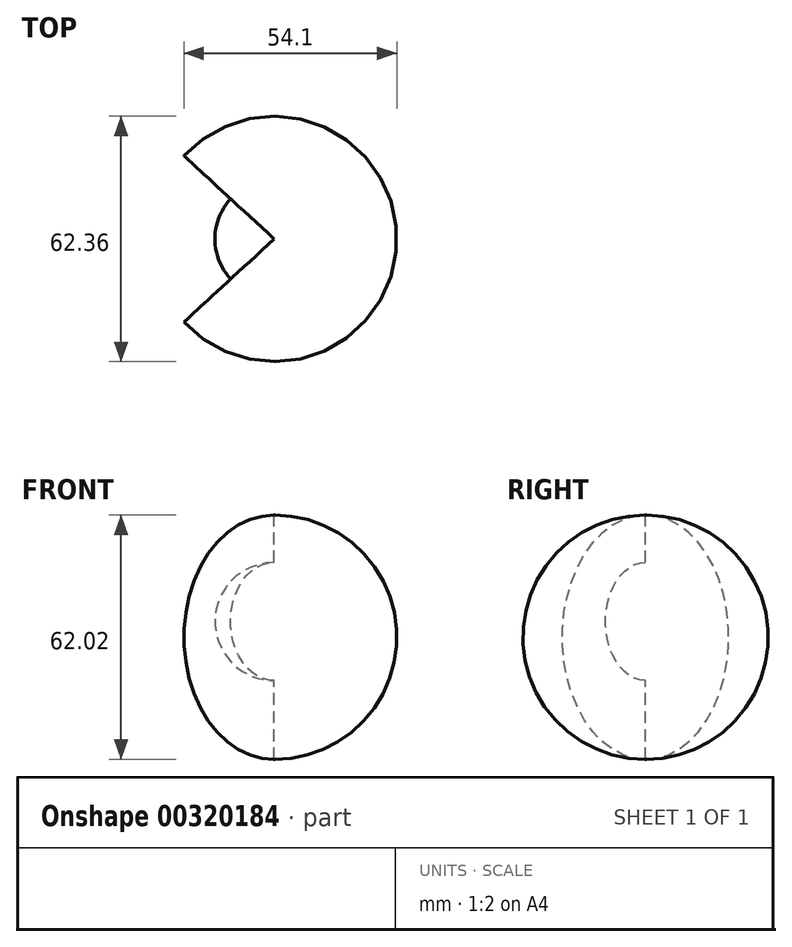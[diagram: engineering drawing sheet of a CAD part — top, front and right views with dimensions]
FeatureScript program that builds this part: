
annotation { "Feature Type Name" : "Feature", "Feature Type Description" : "" }
export const myFeature = defineFeature(function(context is Context, id is Id, definition is map)
    precondition{}
    {
        {
            var Q0;
            Q0=qCreatedBy(makeId("Front.planeOp"),FACE);
            var sketch = newSketch(context, id + "F0", { "sketchPlane" : qUnion([Q0])});
            skLineSegment(sketch, "E0", {"start": v(0, 0) * mm, "end": v(0, 30) * mm});
            skArc(sketch, "E1", {"start": v(0, 0) * mm, "mid": v(15.04, 15) * mm, "end": v(0, 30) * mm});
            skSolve(sketch);
        }
        {
            var Q0;
            Q0 = qSketchRegion(id + "F0", true);
            var Q1;
            Q1=sQuery(id+"F0.wireOp",EDGE,"E0");
            revolve(context, id + "F1", {"entities" : qUnion([Q0]), "axis" : qUnion([Q1]), "revolveType" : RevolveType.FULL});
        }
        {
            var Q0;
            Q0=qCreatedBy(makeId("Front.planeOp"),FACE);
            var sketch = newSketch(context, id + "F2", { "sketchPlane" : qUnion([Q0])});
            skLineSegment(sketch, "E2", {"start": v(0, -20) * mm, "end": v(0, 42.01) * mm});
            skArc(sketch, "E3", {"start": v(0, -20) * mm, "mid": v(31.18, 11) * mm, "end": v(0, 42.01) * mm});
            skSolve(sketch);
        }
        {
            var Q0;
            Q0=makeQuery(id+"F2.imprint","IMPRINT",FACE,{"disambiguationData":[TD([[makeQuery(id+"F2.imprint","IMPRINT",EDGE,{"derivedFrom":sQuery(id+"F2.wireOp",EDGE,"E2")}),-1.0]])]});
            var Q1;
            Q1=sQuery(id+"F2.wireOp",EDGE,"E2");
            var Q2;
            Q2=sQuery(id+"F2.wireOp",EDGE,"E2");
            revolve(context, id + "F3", {"operationType" : NewBodyOperationType.ADD, "entities" : qUnion([Q0]), "surfaceEntities" : qUnion([Q1]), "axis" : qUnion([Q2]), "revolveType" : RevolveType.SYMMETRIC, "angle" : 274.66 * degree});
        }
    });
